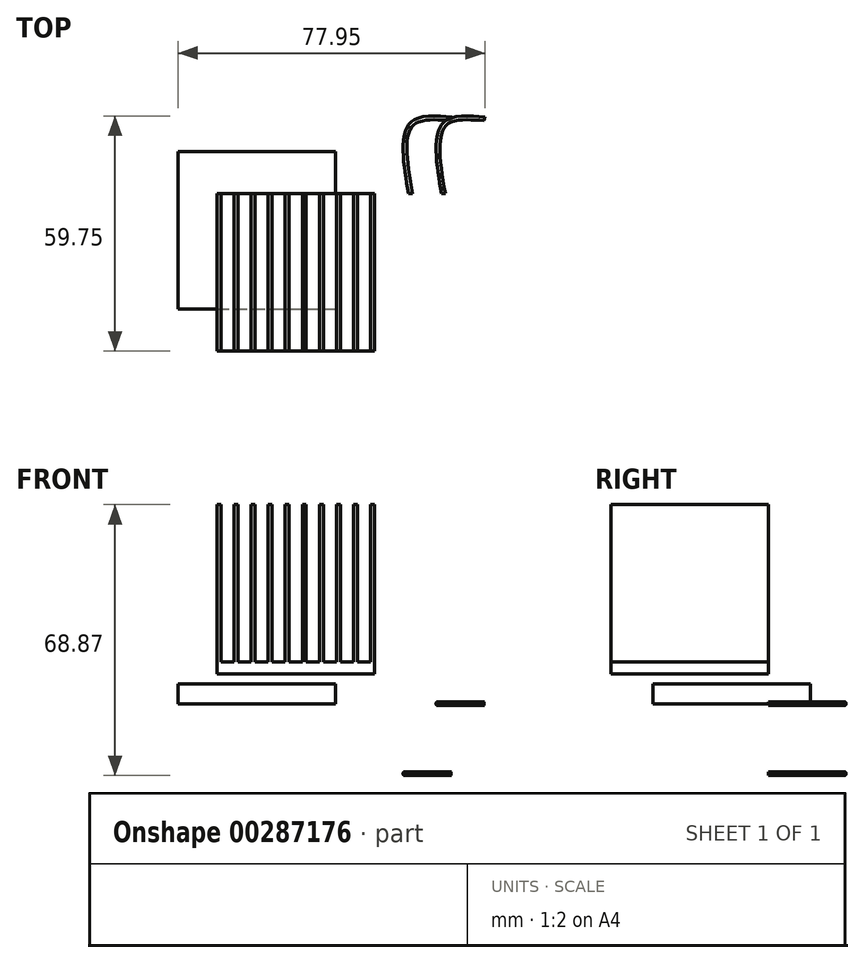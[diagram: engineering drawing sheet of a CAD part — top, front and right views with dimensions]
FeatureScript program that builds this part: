
annotation { "Feature Type Name" : "Feature", "Feature Type Description" : "" }
export const myFeature = defineFeature(function(context is Context, id is Id, definition is map)
    precondition{}
    {
        {
            var Q0;
            Q0=qCreatedBy(makeId("Top.planeOp"),FACE);
            var sketch = newSketch(context, id + "F0", { "sketchPlane" : qUnion([Q0])});
            skLineSegment(sketch, "E0.bottom", {"start": v(-19.42, 10.64) * mm, "end": v(20.58, 10.64) * mm});
            skLineSegment(sketch, "E0.top", {"start": v(-19.42, -29.36) * mm, "end": v(20.58, -29.36) * mm});
            skLineSegment(sketch, "E0.left", {"start": v(-19.42, 10.64) * mm, "end": v(-19.42, -29.36) * mm});
            skLineSegment(sketch, "E0.right", {"start": v(20.58, 10.64) * mm, "end": v(20.58, -29.36) * mm});
            skSolve(sketch);
        }
        {
            var Q0;
            Q0 = qSketchRegion(id + "F0", true);
            extrude(context, id + "F1", {"entities" : qUnion([Q0]), "depth" : 5.08 * mm});
        }
        {
            var Q0;
            Q0=qCreatedBy(makeId("Top.planeOp"),FACE);
            var sketch = newSketch(context, id + "F2", { "sketchPlane" : qUnion([Q0])});
            skFitSpline(sketch, "E1", {"points": [v(47.96, 0) * mm, v(48.06, 17.42) * mm, v(58.4, 19.03) * mm], "startDerivative": vector(-6.44, 38.6) * mm, "endDerivative": vector(28.83, -2.27) * mm});
            skSolve(sketch);
        }
        {
            var Q0;
            Q0=qCreatedBy(makeId("Front.planeOp"),FACE);
            var sketch = newSketch(context, id + "F3", { "sketchPlane" : qUnion([Q0])});
            skCircle(sketch, "E2", {"center": v(47.96, 0) * mm, "radius": 0.5 * mm});
            skSolve(sketch);
        }
        {
            var Q0;
            Q0=makeQuery(id+"F3.imprint","IMPRINT",FACE,{"disambiguationData":[TD([[makeQuery(id+"F3.imprint","IMPRINT",EDGE,{"derivedFrom":sQuery(id+"F3.wireOp",EDGE,"E2")}),1.0]])]});
            var Q1;
            Q1=sQuery(id+"F2.wireOp",EDGE,"E1");
            sweep(context, id + "F4", {"profiles" : qUnion([Q0]), "path" : qUnion([Q1])});
        }
        {
            var Q0;
            Q0=qCreatedBy(makeId("Front.planeOp"),FACE);
            var sketch = newSketch(context, id + "F5", { "sketchPlane" : qUnion([Q0])});
            skLineSegment(sketch, "E3", {"start": v(-8.5, 10.59) * mm, "end": v(-5.18, 10.59) * mm});
            skLineSegment(sketch, "E4", {"start": v(-9.5, 50.59) * mm, "end": v(-9.5, 10.59) * mm});
            skLineSegment(sketch, "E5", {"start": v(-8.5, 50.59) * mm, "end": v(-8.5, 10.59) * mm});
            skLineSegment(sketch, "E6.1.0.0", {"start": v(-4.18, 50.59) * mm, "end": v(-4.18, 10.59) * mm});
            skLineSegment(sketch, "E6.1.0.1", {"start": v(-5.18, 50.59) * mm, "end": v(-5.18, 10.59) * mm});
            skLineSegment(sketch, "E6.direction1", {"start": v(-8.5, 10.59) * mm, "end": v(-5.18, 10.59) * mm, "construction": true});
            skLineSegment(sketch, "E7.trimOffspring", {"start": v(-8.5, 50.59) * mm, "end": v(-9.5, 50.59) * mm});
            skLineSegment(sketch, "E8.trimOffspring", {"start": v(-4.18, 50.59) * mm, "end": v(-5.18, 50.59) * mm});
            skLineSegment(sketch, "E9.trimOffspring", {"start": v(8.8, 50.59) * mm, "end": v(8.8, 50.59) * mm});
            skLineSegment(sketch, "E10", {"start": v(-9.5, 10.59) * mm, "end": v(-9.5, 7.59) * mm});
            skLineSegment(sketch, "E11", {"start": v(-9.5, 7.59) * mm, "end": v(30.5, 7.59) * mm});
            skLineSegment(sketch, "E12", {"start": v(30.5, 10.59) * mm, "end": v(30.5, 7.59) * mm});
            skLineSegment(sketch, "E13.0.2.0", {"start": v(0.15, 50.59) * mm, "end": v(0.15, 10.59) * mm});
            skLineSegment(sketch, "E13.3.2.0", {"start": v(-0.85, 50.59) * mm, "end": v(-0.85, 10.59) * mm});
            skLineSegment(sketch, "E13.0.3.0", {"start": v(4.48, 50.59) * mm, "end": v(4.48, 10.59) * mm});
            skLineSegment(sketch, "E13.3.3.0", {"start": v(3.48, 50.59) * mm, "end": v(3.48, 10.59) * mm});
            skLineSegment(sketch, "E13.0.4.0", {"start": v(8.8, 50.59) * mm, "end": v(8.8, 10.59) * mm});
            skLineSegment(sketch, "E13.3.4.0", {"start": v(7.8, 50.59) * mm, "end": v(7.8, 10.59) * mm});
            skLineSegment(sketch, "E14.0.5.0", {"start": v(13.13, 50.59) * mm, "end": v(13.13, 10.59) * mm});
            skLineSegment(sketch, "E14.3.5.0", {"start": v(12.13, 50.59) * mm, "end": v(12.13, 10.59) * mm});
            skLineSegment(sketch, "E14.0.6.0", {"start": v(17.46, 50.59) * mm, "end": v(17.46, 10.59) * mm});
            skLineSegment(sketch, "E14.3.6.0", {"start": v(16.46, 50.59) * mm, "end": v(16.46, 10.59) * mm});
            skLineSegment(sketch, "E14.0.7.0", {"start": v(21.79, 50.59) * mm, "end": v(21.79, 10.59) * mm});
            skLineSegment(sketch, "E14.3.7.0", {"start": v(20.79, 50.59) * mm, "end": v(20.79, 10.59) * mm});
            skLineSegment(sketch, "E15.0.8.0", {"start": v(26.11, 50.59) * mm, "end": v(26.11, 10.59) * mm});
            skLineSegment(sketch, "E15.3.8.0", {"start": v(25.11, 50.59) * mm, "end": v(25.11, 10.59) * mm});
            skLineSegment(sketch, "E15.0.9.0", {"start": v(30.44, 50.59) * mm, "end": v(30.44, 10.59) * mm});
            skLineSegment(sketch, "E15.3.9.0", {"start": v(29.44, 50.59) * mm, "end": v(29.44, 10.59) * mm});
            skLineSegment(sketch, "E16", {"start": v(29.44, 10.59) * mm, "end": v(26.11, 10.59) * mm});
            skLineSegment(sketch, "E17", {"start": v(25.11, 10.59) * mm, "end": v(21.79, 10.59) * mm});
            skLineSegment(sketch, "E18", {"start": v(16.46, 10.59) * mm, "end": v(13.13, 10.59) * mm});
            skLineSegment(sketch, "E19", {"start": v(12.13, 10.59) * mm, "end": v(8.8, 10.59) * mm});
            skLineSegment(sketch, "E20", {"start": v(7.8, 10.59) * mm, "end": v(4.48, 10.59) * mm});
            skLineSegment(sketch, "E21", {"start": v(-0.85, 10.59) * mm, "end": v(-4.18, 10.59) * mm});
            skLineSegment(sketch, "E22.trimOffspring", {"start": v(20.79, 10.59) * mm, "end": v(17.46, 10.59) * mm});
            skLineSegment(sketch, "E23.trimOffspring", {"start": v(3.48, 10.59) * mm, "end": v(0.15, 10.59) * mm});
            skLineSegment(sketch, "E24", {"start": v(30.5, 10.59) * mm, "end": v(30.44, 10.59) * mm});
            skLineSegment(sketch, "E25.trimOffspring", {"start": v(26.11, 50.59) * mm, "end": v(25.11, 50.59) * mm});
            skLineSegment(sketch, "E26.trimOffspring", {"start": v(17.46, 50.59) * mm, "end": v(16.46, 50.59) * mm});
            skLineSegment(sketch, "E27.trimOffspring", {"start": v(13.13, 50.59) * mm, "end": v(12.13, 50.59) * mm});
            skLineSegment(sketch, "E28.trimOffspring", {"start": v(8.8, 50.59) * mm, "end": v(7.8, 50.59) * mm});
            skLineSegment(sketch, "E29.trimOffspring", {"start": v(21.79, 50.59) * mm, "end": v(20.79, 50.59) * mm});
            skLineSegment(sketch, "E30.trimOffspring", {"start": v(4.48, 50.59) * mm, "end": v(3.48, 50.59) * mm});
            skLineSegment(sketch, "E31.trimOffspring", {"start": v(0.15, 50.59) * mm, "end": v(-0.85, 50.59) * mm});
            skLineSegment(sketch, "E32", {"start": v(30.44, 50.59) * mm, "end": v(29.44, 50.59) * mm});
            skSolve(sketch);
        }
        {
            var Q0;
            Q0 = qSketchRegion(id + "F5", true);
            extrude(context, id + "F6", {"entities" : qUnion([Q0]), "depth" : 40 * mm});
        }
        {
            var Q0;
            Q0=makeQuery(id+"F4.opSweep","SWEPT_BODY",BODY,{"disambiguationData":[OSD([sQuery(id+"F2.wireOp",EDGE,"E1"),sQuery(id+"F3.wireOp",EDGE,"E2")])]});
            transform(context, id + "F7", {"entities" : qUnion([Q0]), "transformType" : TransformType.TRANSLATION_3D, "dx" : -8.38 * mm, "dy" : 0 * mm, "dz" : -17.78 * mm, "makeCopy" : true});
        }
        {
            var Q0;
            Q0=makeQuery(id+"F1.opExtrude","SWEPT_FACE",FACE,{"disambiguationData":[OSD([sQuery(id+"F0.wireOp",EDGE,"E0.bottom")])]});
            var sketch = newSketch(context, id + "F8", { "sketchPlane" : qUnion([Q0])});
            skLineSegment(sketch, "E33", {"start": v(-7.88, 5.08) * mm, "end": v(-7.88, 0) * mm, "construction": true});
            skLineSegment(sketch, "E34", {"start": v(6.72, 5.08) * mm, "end": v(6.72, 0) * mm, "construction": true});
            skSolve(sketch);
        }
    });
